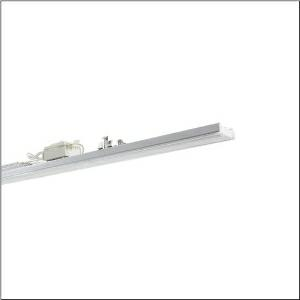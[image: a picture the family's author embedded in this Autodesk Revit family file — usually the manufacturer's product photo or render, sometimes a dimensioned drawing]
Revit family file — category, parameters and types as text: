
# Revit family: licross_r__21_recessed_mo_52tl127n485g_113a
name_source: partatom
category: Lighting Fixtures
units: mm (PartAtom-declared; Revit-internal decimal feet)

## family parameters
Cut with Voids When Loaded = No
Host = Face
Light Source = No
Part Type = Normal
Room Calculation Point = No
Round Connector Dimension = Use Diameter
Shared = No

## types (1)
- Licross® 21 Recessed MO (1 x LED, 8820 lm, 47.9 W, 4000K)
    Apparent Load = 48 VA
    CIE Flux Codes = 72 92 99 100 100
    Color Rendering = 80
    Color Temperature = 4000K
    Default Elevation = 1800 mm
    Description = Licross® 21 Recessed MO, luminaire insert, of sheet steel, galvanised, coil coated, white, length: 1.500mm, width: 66mm, height: 67mm, LED rated luminous flux: 8.820lm, light colour: 840, control gear: ON/OFF, with plug, 3-pole, with phase selection, mains connection: 220..240V, AC, 50/60Hz, rated input power: 48W, internal wiring halogen-free, primary optical cover: cover, of PMMA, light emission: direct distribution, primary light characteristic: symmetric, protection rating (complete): IP40, insulation class (complete): insulation class I (protective earthing), certification: CE, ENEC, VDE, UKCA, protection symbol: D if used in an environment without relevant dust loads with corresponding accessories, impact resistance: IK06, permissible ambient temperature for indoor applications: -35..+40°C, corresponds to IFS (International Featured Standards) requirements for safety and quality in the food industry, reducing of maximum allowable ambient temperature of 5°C with ceiling mounting, LABS conformity tested according to VDMA 24364:2018-05, packaging unit: 1 piece
    Height = 58 mm
    Lamp = 1 x LED
    Lamp Light Flux = 8820 lm
    Lamp Power = 47.9 W
    Lamp count = 1
    Length = 1500 mm
    Luminous efficacy = 184 lm/W
    Manufacturer = Siteco
    ModVariant = No
    Model = 52TL127N485G
    Mounting Place = Ceiling
    Mounting Type = Pendant
    Number of Poles = 1
    OnlyDefault = Yes
    Power Factor = 1
    Product Name = Licross® 21 Recessed MO
    Product group = luminaire insert | ceiling pendant
    ProductGroupID = 902
    Protection Class = Protection class I
    Protection Degree = IP 40
    RLX_Detail_Level = 1
    RLX_Emergency_Light_Flux = 0 lm
    RLX_Emergency_Type = 0
    RLX_Emergency_Type_DB = No
    RlxData = <blob elided: 20949 chars, md5=d3080e25>
    Socket = socket
    Standby Power = 0 W
    System Light Flux = 8820 lm
    System Power = 48 W
    Type Comments = Product without accessories
    Type Image = l_1296930.jpg
    URL = http://relux.com
    VarID = ---
    Voltage = 0 V
    Weight = 0.00 kg
    Width = 66 mm

## geometry (parser evidence)
native form markers: Blend x4, Sweep x10
no freeform markers — native parametric forms only
